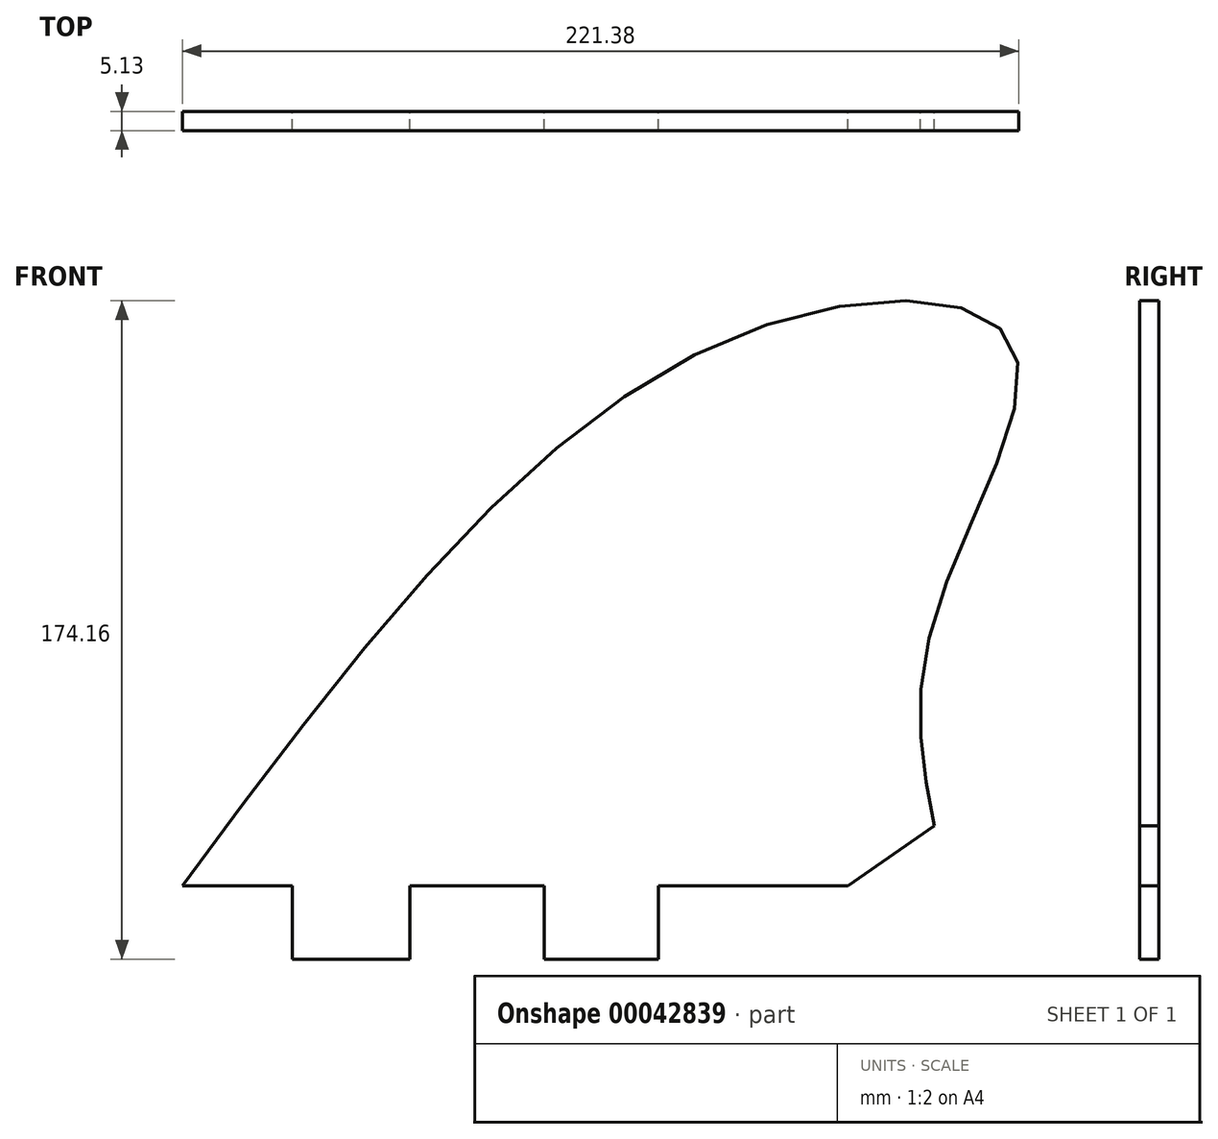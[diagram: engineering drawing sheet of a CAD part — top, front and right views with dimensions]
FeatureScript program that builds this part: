
annotation { "Feature Type Name" : "Feature", "Feature Type Description" : "" }
export const myFeature = defineFeature(function(context is Context, id is Id, definition is map)
    precondition{}
    {
        {
            var Q0;
            Q0=qCreatedBy(makeId("Front.planeOp"),FACE);
            var sketch = newSketch(context, id + "F0", { "sketchPlane" : qUnion([Q0])});
            skLineSegment(sketch, "E0", {"start": v(-75.5, -39.07) * mm, "end": v(-46.4, -39.07) * mm});
            skLineSegment(sketch, "E1", {"start": v(-46.4, -39.07) * mm, "end": v(-46.4, -58.4) * mm});
            skLineSegment(sketch, "E2", {"start": v(-46.4, -58.4) * mm, "end": v(-15.26, -58.4) * mm});
            skLineSegment(sketch, "E3", {"start": v(-15.26, -58.4) * mm, "end": v(-15.26, -39.07) * mm});
            skLineSegment(sketch, "E4", {"start": v(-15.26, -39.07) * mm, "end": v(20.35, -39.07) * mm});
            skLineSegment(sketch, "E5", {"start": v(20.35, -39.07) * mm, "end": v(20.35, -58.4) * mm});
            skLineSegment(sketch, "E6", {"start": v(20.35, -58.4) * mm, "end": v(50.47, -58.4) * mm});
            skLineSegment(sketch, "E7", {"start": v(50.47, -58.4) * mm, "end": v(50.47, -39.07) * mm});
            skLineSegment(sketch, "E8", {"start": v(50.47, -39.07) * mm, "end": v(100.73, -39.07) * mm});
            skLineSegment(sketch, "E9", {"start": v(100.73, -39.07) * mm, "end": v(123.52, -23.2) * mm});
            skFitSpline(sketch, "E10", {"points": [v(123.52, -23.2) * mm, v(123.52, 31.75) * mm, v(144.28, 103.99) * mm, v(67.15, 104.8) * mm, v(-75.5, -39.07) * mm], "startDerivative": vector(-50.87, 264.98) * mm, "endDerivative": vector(-367.02, -496.03) * mm});
            skSolve(sketch);
        }
        {
            var Q0;
            Q0=makeQuery(id+"F0.imprint","IMPRINT",FACE,{"disambiguationData":[TD([[makeQuery(id+"F0.imprint","IMPRINT",EDGE,{"derivedFrom":sQuery(id+"F0.wireOp",EDGE,"E0")}),1.0]])]});
            extrude(context, id + "F1", {"entities" : qUnion([Q0]), "depth" : 5.13 * mm});
        }
    });
